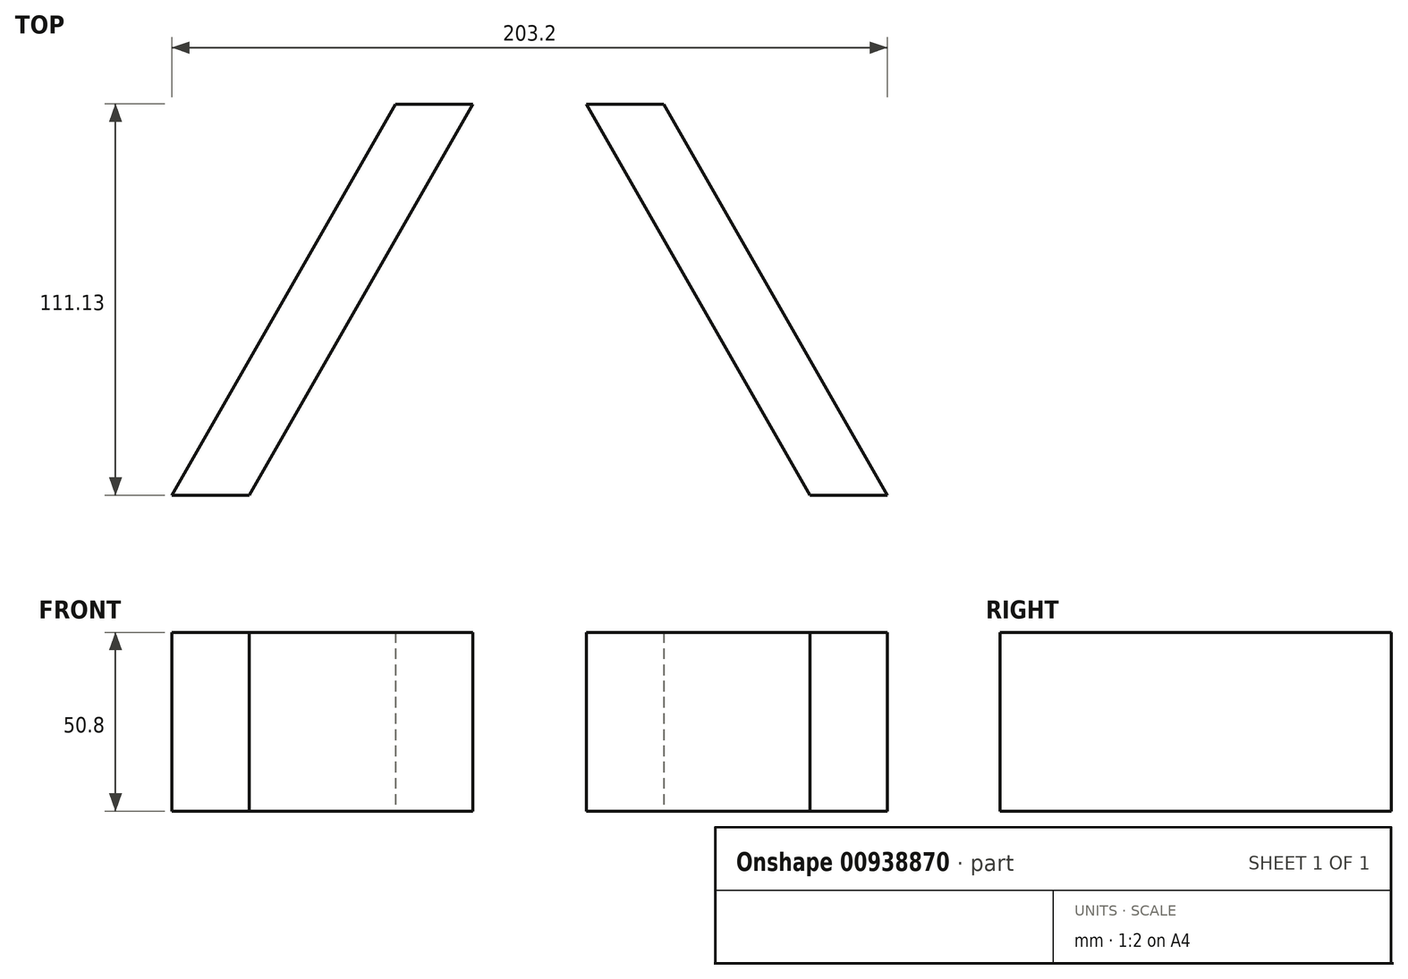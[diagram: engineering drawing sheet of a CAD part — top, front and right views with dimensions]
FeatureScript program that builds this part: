
annotation { "Feature Type Name" : "Feature", "Feature Type Description" : "" }
export const myFeature = defineFeature(function(context is Context, id is Id, definition is map)
    precondition{}
    {
        {
            var Q0;
            Q0=qCreatedBy(makeId("Top.planeOp"),FACE);
            var sketch = newSketch(context, id + "F0", { "sketchPlane" : qUnion([Q0])});
            skLineSegment(sketch, "E0", {"start": v(-101.6, 0) * mm, "end": v(101.6, 0) * mm, "construction": true});
            skLineSegment(sketch, "E1", {"start": v(-101.6, 0) * mm, "end": v(0, 177.8) * mm, "construction": true});
            skLineSegment(sketch, "E2", {"start": v(0, 177.8) * mm, "end": v(101.6, 0) * mm, "construction": true});
            skLineSegment(sketch, "E3.bottom", {"start": v(38.1, 139.7) * mm, "end": v(-38.1, 139.7) * mm, "construction": true});
            skLineSegment(sketch, "E3.top", {"start": v(38.1, 215.9) * mm, "end": v(-38.1, 215.9) * mm, "construction": true});
            skLineSegment(sketch, "E3.left", {"start": v(38.1, 139.7) * mm, "end": v(38.1, 215.9) * mm, "construction": true});
            skLineSegment(sketch, "E3.right", {"start": v(-38.1, 139.7) * mm, "end": v(-38.1, 215.9) * mm, "construction": true});
            skPoint(sketch, "E3.middle", {"position": v(0, 177.8) * mm});
            skLineSegment(sketch, "E4", {"start": v(38.1, 139.7) * mm, "end": v(38.1, 111.12) * mm, "construction": true});
            skLineSegment(sketch, "E5", {"start": v(-38.1, 139.7) * mm, "end": v(-38.1, 111.13) * mm, "construction": true});
            skLineSegment(sketch, "E6", {"start": v(-101.6, 0) * mm, "end": v(-79.66, 0) * mm});
            skLineSegment(sketch, "E7", {"start": v(-79.66, 0) * mm, "end": v(-16.16, 111.13) * mm});
            skLineSegment(sketch, "E8", {"start": v(-38.1, 111.13) * mm, "end": v(-16.16, 111.13) * mm});
            skLineSegment(sketch, "E9", {"start": v(0, 177.8) * mm, "end": v(0, 0) * mm, "construction": true});
            skLineSegment(sketch, "E10.MirrorCS", {"start": v(38.1, 111.13) * mm, "end": v(16.16, 111.13) * mm});
            skLineSegment(sketch, "E11.MirrorCS", {"start": v(79.66, 0) * mm, "end": v(16.16, 111.13) * mm});
            skLineSegment(sketch, "E12.MirrorCS", {"start": v(101.6, 0) * mm, "end": v(-101.6, 0) * mm, "construction": true});
            skLineSegment(sketch, "E13.MirrorCS", {"start": v(101.6, 0) * mm, "end": v(79.66, 0) * mm});
            skLineSegment(sketch, "E14", {"start": v(-101.6, 0) * mm, "end": v(-38.1, 111.13) * mm});
            skLineSegment(sketch, "E15", {"start": v(38.1, 111.12) * mm, "end": v(101.6, 0) * mm});
            skSolve(sketch);
        }
        {
            var Q0;
            Q0=makeQuery(id+"F0.imprint","IMPRINT",FACE,{"disambiguationData":[TD([[makeQuery(id+"F0.imprint","IMPRINT",EDGE,{"derivedFrom":sQuery(id+"F0.wireOp",EDGE,"E6")}),1.0]])]});
            var Q1;
            Q1=makeQuery(id+"F0.imprint","IMPRINT",FACE,{"disambiguationData":[TD([[makeQuery(id+"F0.imprint","IMPRINT",EDGE,{"derivedFrom":sQuery(id+"F0.wireOp",EDGE,"E10.MirrorCS")}),1.0]])]});
            extrude(context, id + "F1", {"entities" : qUnion([Q0, Q1]), "depth" : 50.8 * mm, "offsetDistance" : 25.4 * mm});
        }
    });
